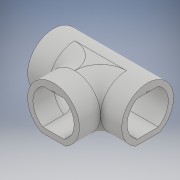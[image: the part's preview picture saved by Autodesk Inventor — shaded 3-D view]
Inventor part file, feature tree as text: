
AUTODESK INVENTOR PART (.ipt)
format: ipt  version: 2017 (Build 210142000, 142)  size: 465,920 bytes
history: native  units: in
note: dims shown in document units (in); Inventor stores cm internally (conversion verified against a paired STEP export)
features: extrude x11, sketch x8, plane x2, sweep x2, mirror x2, other x1, fillet x1
ambient origin geometry x8: Origin, YZ Plane, XZ Plane, XY Plane, X Axis, Y Axis, Z Axis, Center Point
bodies: Solid1 (feature_tree), Solid2 (feature_tree), Solid3 (feature_tree), Solid4 (feature_tree), Solid5 (feature_tree), Solid6 (feature_tree)
feature tree (27):
  sketch  "Sketch1"  dims[d0=6.6667in d1=4.0in d2=9.7746in d3=4.0in d4=0.0in d5=-4.8873in]
  extrude  "corridor"  [1 undecoded]
  extrude  "light right of T"  Depth=4.0in TaperAngle=0.0deg
  plane  "Work Plane1"
  sketch  "Sketch4"  dims[d6=6.6667in d7=4.0in d8=9.7746in d10=4.0in d11=0.0in]
  extrude  "T bottom"  TaperAngle=0.0deg  [1 undecoded]
  extrude  "light bottom of T"  TaperAngle=0.0deg  [1 undecoded]
  sketch  "Sketch8"  dims[d22=9.7746in d23=0.0in]
  sketch  "Sketch7"  dims[d19=4.8873in d20=0.0in d21=0.0in]
  sweep  "corner curve"
  sweep  "light curve right"
  extrude  "flat of T"  Depth=0.0625in
  extrude  "light flat of T"  Depth=0.0892in
  sketch  "Sketch10"  dims[d25=4.0in d26=9.7746in d31=1.0in d32=0.0in]
  mirror  "mirror plane"
  extrude  "other end of T"  Depth=0.0625in TaperAngle=0.0deg
  extrude  "other end of T light"  Depth=0.0625in TaperAngle=0.0deg
  mirror  "corner curve mirror"
  other  "light curve left"
  plane  "Work Plane3"
  extrude  "top hole fill"  TaperAngle=0.0deg  [1 undecoded]
  extrude  "Extrusion18"  Depth=0.0625in TaperAngle=0.0deg
  fillet  "Fillet1"  Radius=4.0in
  extrude  "bottom hole fill"  Depth=0.0625in TaperAngle=0.0deg
  sketch  "Sketch12"  dims[d41=1.0in d42=1.0in]
  sketch  "Sketch15"  dims[d56=0.5833in d57=0.0625in d58=0.0625in d59=0.125in]
  sketch  "Sketch16"  dims[d65=0.25in d66=0.125in d67=45.0deg d68=0.0892in d69=0.0884in d88=0.5833in d89=0.0625in d90=0.0625in d91=0.125in d92=0.25in d93=0.125in d95=0.0892in d96=0.0884in d97=1.0in d98=0.0in d99=1.0in d100=0.0in d101=0.0in d102=0.0in d103=1.0in d104=0.0in d105=4.0in d106=0.0in d107=4.0in d108=0.0in d109=90.0deg d110=3.3333in d112=1.429in d115=4.0in d116=0.0in d117=10.3167in d118=10.3167in d119=0.0417in d120=0.125in d121=0.0in d122=0.0625in]
note: 4 required parameter values undecoded (feature->parameter linkage not recoverable at this tier; creation-order binding heuristic only, values carry confidence <= 0.55)
